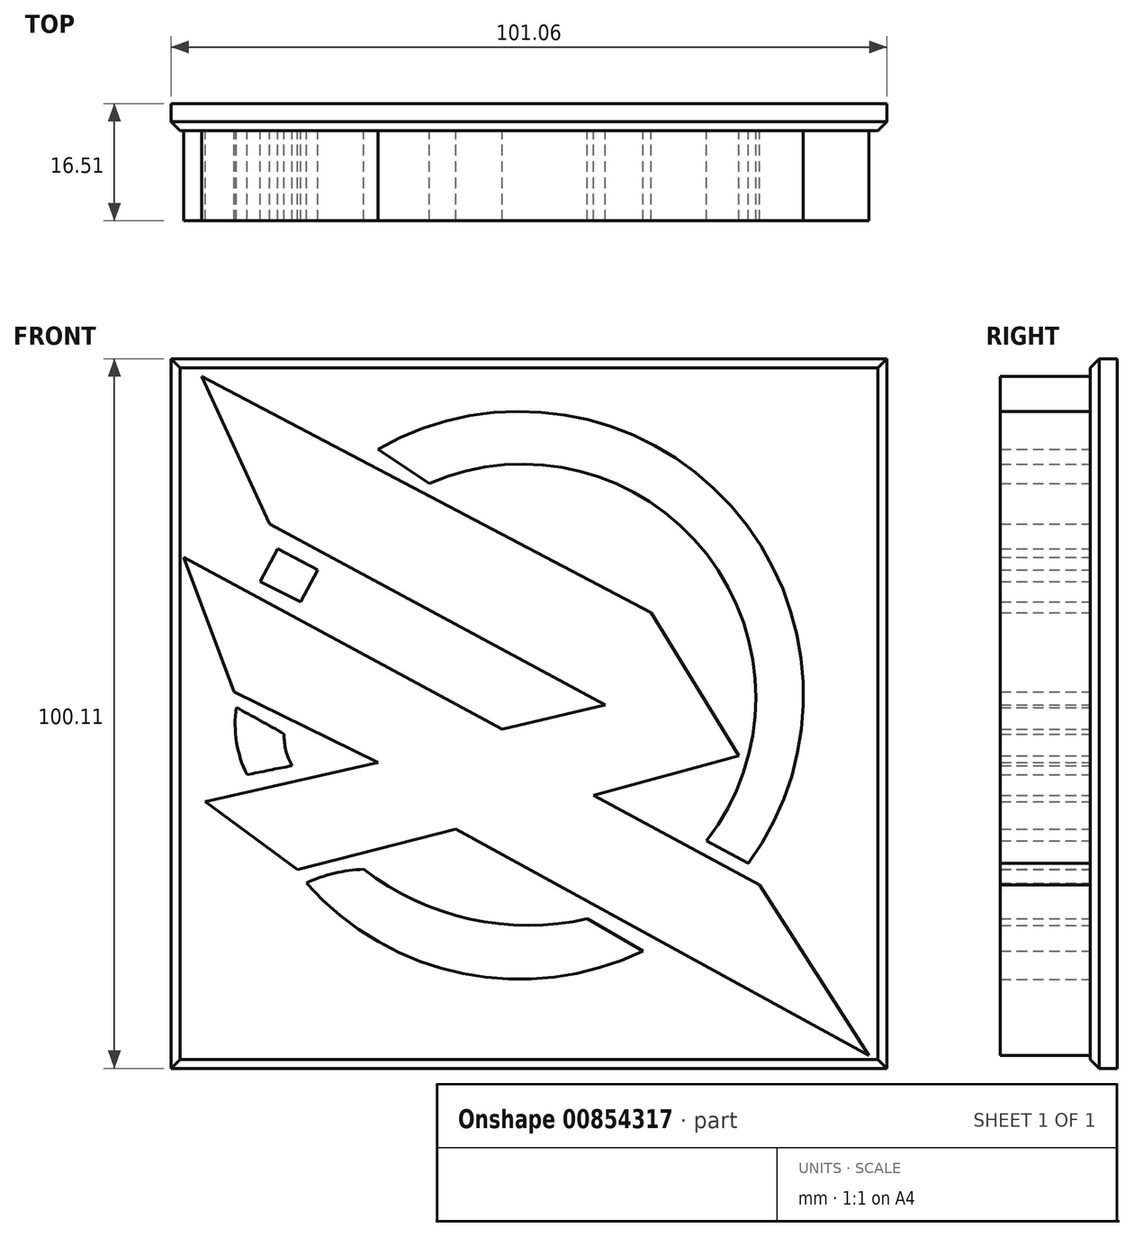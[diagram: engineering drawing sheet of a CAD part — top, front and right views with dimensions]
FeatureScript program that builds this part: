
annotation { "Feature Type Name" : "Feature", "Feature Type Description" : "" }
export const myFeature = defineFeature(function(context is Context, id is Id, definition is map)
    precondition{}
    {
        {
            var Q0;
            Q0=qCreatedBy(makeId("Front.planeOp"),FACE);
            var sketch = newSketch(context, id + "F0", { "sketchPlane" : qUnion([Q0])});
            skLineSegment(sketch, "E0", {"start": v(-59.3, 47.9) * mm, "end": v(4.16, 14.55) * mm});
            skLineSegment(sketch, "E1", {"start": v(4.16, 14.55) * mm, "end": v(16.56, -5.63) * mm});
            skLineSegment(sketch, "E2", {"start": v(16.56, -5.63) * mm, "end": v(-3.96, -11.27) * mm});
            skLineSegment(sketch, "E3", {"start": v(-3.96, -11.27) * mm, "end": v(19.5, -23.9) * mm});
            skLineSegment(sketch, "E4", {"start": v(19.5, -23.9) * mm, "end": v(34.87, -47.92) * mm});
            skLineSegment(sketch, "E5", {"start": v(34.87, -47.92) * mm, "end": v(-23.42, -16.04) * mm});
            skLineSegment(sketch, "E6", {"start": v(-23.42, -16.04) * mm, "end": v(-45.77, -21.75) * mm});
            skLineSegment(sketch, "E7", {"start": v(-45.77, -21.75) * mm, "end": v(-58.78, -12.17) * mm});
            skLineSegment(sketch, "E8", {"start": v(-58.78, -12.17) * mm, "end": v(-34.38, -6.6) * mm});
            skLineSegment(sketch, "E9", {"start": v(-34.38, -6.6) * mm, "end": v(-54.72, 3.38) * mm});
            skLineSegment(sketch, "E10", {"start": v(-54.72, 3.38) * mm, "end": v(-61.85, 22.32) * mm});
            skLineSegment(sketch, "E11", {"start": v(-61.85, 22.32) * mm, "end": v(-16.89, -1.91) * mm});
            skLineSegment(sketch, "E12", {"start": v(-16.89, -1.91) * mm, "end": v(-2.3, 1.51) * mm});
            skLineSegment(sketch, "E13", {"start": v(-2.3, 1.51) * mm, "end": v(-49.7, 27.04) * mm});
            skLineSegment(sketch, "E14", {"start": v(-49.7, 27.04) * mm, "end": v(-59.3, 47.9) * mm});
            skArc(sketch, "E15", {"start": v(-47.62, -2.6) * mm, "mid": v(-47.38, -4.92) * mm, "end": v(-46.5, -7.07) * mm});
            skArc(sketch, "E16", {"start": v(-47.62, -2.6) * mm, "mid": v(-50.99, -0.7) * mm, "end": v(-54.4, 1.14) * mm});
            skArc(sketch, "E17", {"start": v(-54.4, 1.14) * mm, "mid": v(-54.36, -3.72) * mm, "end": v(-52.88, -8.35) * mm});
            skArc(sketch, "E18", {"start": v(-46.5, -7.07) * mm, "mid": v(-49.7, -7.7) * mm, "end": v(-52.88, -8.35) * mm});
            skArc(sketch, "E19", {"start": v(-44.5, -23.6) * mm, "mid": v(-22.35, -36.42) * mm, "end": v(3.04, -33.21) * mm});
            skLineSegment(sketch, "E20", {"start": v(3.04, -33.21) * mm, "end": v(-4.83, -28.67) * mm});
            skArc(sketch, "E21", {"start": v(-36.42, -21.67) * mm, "mid": v(-21.4, -28.7) * mm, "end": v(-4.83, -28.67) * mm});
            skArc(sketch, "E22", {"start": v(-36.42, -21.67) * mm, "mid": v(-40.55, -22.25) * mm, "end": v(-44.5, -23.6) * mm});
            skLineSegment(sketch, "E23", {"start": v(17.88, -20.86) * mm, "end": v(11.97, -17.68) * mm});
            skArc(sketch, "E24", {"start": v(11.97, -17.68) * mm, "mid": v(12.02, 22.77) * mm, "end": v(-27.18, 32.75) * mm});
            skLineSegment(sketch, "E25", {"start": v(-34.38, 37.6) * mm, "end": v(-27.18, 32.75) * mm});
            skLineSegment(sketch, "E26", {"start": v(-45.34, 16.04) * mm, "end": v(-42.9, 20.55) * mm});
            skLineSegment(sketch, "E27", {"start": v(-42.9, 20.55) * mm, "end": v(-48.57, 23.53) * mm});
            skLineSegment(sketch, "E28", {"start": v(-48.57, 23.53) * mm, "end": v(-51, 18.91) * mm});
            skLineSegment(sketch, "E29", {"start": v(-51, 18.91) * mm, "end": v(-45.34, 16.04) * mm});
            skArc(sketch, "E30.trimOffspring", {"start": v(17.88, -20.86) * mm, "mid": v(15.46, 29.56) * mm, "end": v(-34.38, 37.6) * mm});
            skLineSegment(sketch, "E31", {"start": v(-27.18, 32.75) * mm, "end": v(-28.04, 31.47) * mm});
            skLineSegment(sketch, "E32", {"start": v(-27.93, 33.26) * mm, "end": v(-28.85, 31.9) * mm});
            skLineSegment(sketch, "E33", {"start": v(-34.38, 37.6) * mm, "end": v(-35.78, 35.53) * mm});
            skLineSegment(sketch, "E34", {"start": v(-33.82, 37.23) * mm, "end": v(-35.18, 35.22) * mm});
            skLineSegment(sketch, "E35", {"start": v(-49.7, 27.04) * mm, "end": v(-48.57, 23.53) * mm});
            skLineSegment(sketch, "E36", {"start": v(-51, 18.91) * mm, "end": v(-52.02, 17.02) * mm});
            skLineSegment(sketch, "E37", {"start": v(-50, 18.4) * mm, "end": v(-51.03, 16.49) * mm});
            skLineSegment(sketch, "E38", {"start": v(-54.72, 3.38) * mm, "end": v(-54.4, 1.14) * mm});
            skLineSegment(sketch, "E39", {"start": v(-53.62, 2.84) * mm, "end": v(-53.3, 0.56) * mm});
            skLineSegment(sketch, "E40", {"start": v(-47.5, 25.85) * mm, "end": v(-47.2, 22.81) * mm});
            skLineSegment(sketch, "E41", {"start": v(-44.5, -23.6) * mm, "end": v(-45.77, -21.75) * mm});
            skLineSegment(sketch, "E42", {"start": v(-44.03, -21.3) * mm, "end": v(-43.55, -23.2) * mm});
            skLineSegment(sketch, "E43", {"start": v(17.88, -20.86) * mm, "end": v(19.5, -23.9) * mm});
            skLineSegment(sketch, "E44", {"start": v(16.73, -20.24) * mm, "end": v(16.51, -22.3) * mm});
            skSolve(sketch);
        }
        {
            var Q0;
            {var subQ18=sQuery(id+"F0.wireOp",EDGE,"E1");Q0=makeQuery(id+"F0.imprint","IMPRINT",FACE,{"disambiguationData":[TD([[makeQuery(id+"F0.imprint","IMPRINT",EDGE,{"derivedFrom":subQ18}),-1.0]])]});}
            var Q1;
            {var subQ3=sQuery(id+"F0.wireOp",EDGE,"E15");Q1=makeQuery(id+"F0.imprint","IMPRINT",FACE,{"disambiguationData":[TD([[makeQuery(id+"F0.imprint","IMPRINT",EDGE,{"derivedFrom":subQ3}),-1.0]])]});}
            var Q2;
            {var subQ3=sQuery(id+"F0.wireOp",EDGE,"E26");Q2=makeQuery(id+"F0.imprint","IMPRINT",FACE,{"disambiguationData":[TD([[makeQuery(id+"F0.imprint","IMPRINT",EDGE,{"derivedFrom":subQ3}),1.0]])]});}
            var Q3;
            {var subQ3=sQuery(id+"F0.wireOp",EDGE,"E24");Q3=makeQuery(id+"F0.imprint","IMPRINT",FACE,{"disambiguationData":[TD([[makeQuery(id+"F0.imprint","IMPRINT",EDGE,{"derivedFrom":subQ3}),-1.0]])]});}
            var Q4;
            {var subQ3=sQuery(id+"F0.wireOp",EDGE,"E19");Q4=makeQuery(id+"F0.imprint","IMPRINT",FACE,{"disambiguationData":[TD([[makeQuery(id+"F0.imprint","IMPRINT",EDGE,{"derivedFrom":subQ3}),1.0]])]});}
            extrude(context, id + "F1", {"entities" : qUnion([Q0, Q1, Q2, Q3, Q4]), "depth" : 12.7 * mm, "offsetDistance" : 25.4 * mm});
        }
        {
            var Q0;
            Q0=makeQuery(id+"F1.opExtrude","CAP_FACE",FACE,{"disambiguationData":[OSD([sQuery(id+"F0.wireOp",EDGE,"E0"),sQuery(id+"F0.wireOp",EDGE,"E1"),sQuery(id+"F0.wireOp",EDGE,"E2"),sQuery(id+"F0.wireOp",EDGE,"E3"),sQuery(id+"F0.wireOp",EDGE,"E4"),sQuery(id+"F0.wireOp",EDGE,"E5"),sQuery(id+"F0.wireOp",EDGE,"E6"),sQuery(id+"F0.wireOp",EDGE,"E7"),sQuery(id+"F0.wireOp",EDGE,"E8"),sQuery(id+"F0.wireOp",EDGE,"E9"),sQuery(id+"F0.wireOp",EDGE,"E10"),sQuery(id+"F0.wireOp",EDGE,"E11"),sQuery(id+"F0.wireOp",EDGE,"E12"),sQuery(id+"F0.wireOp",EDGE,"E13"),sQuery(id+"F0.wireOp",EDGE,"E14")])],"isStart":true});
            var sketch = newSketch(context, id + "F2", { "sketchPlane" : qUnion([Q0])});
            skLineSegment(sketch, "E45.bottom", {"start": v(-37.45, -49.77) * mm, "end": v(63.6, -49.77) * mm});
            skLineSegment(sketch, "E45.top", {"start": v(-37.45, 50.34) * mm, "end": v(63.6, 50.34) * mm});
            skLineSegment(sketch, "E45.left", {"start": v(-37.45, -49.77) * mm, "end": v(-37.45, 50.34) * mm});
            skLineSegment(sketch, "E45.right", {"start": v(63.6, -49.77) * mm, "end": v(63.6, 50.34) * mm});
            skSolve(sketch);
        }
        {
            var Q0;
            Q0 = qSketchRegion(id + "F2", true);
            extrude(context, id + "F3", {"entities" : qUnion([Q0]), "depth" : 3.8 * mm, "offsetDistance" : 25.4 * mm});
        }
        {
            var Q0;
            Q0=makeQuery(id+"F3.opExtrude","CAP_EDGE",EDGE,{"disambiguationData":[OSD([sQuery(id+"F2.wireOp",EDGE,"E45.top")])],"isStart":true});
            var Q1;
            Q1=makeQuery(id+"F3.opExtrude","CAP_EDGE",EDGE,{"disambiguationData":[OSD([sQuery(id+"F2.wireOp",EDGE,"E45.right")])],"isStart":true});
            var Q2;
            Q2=makeQuery(id+"F3.opExtrude","CAP_EDGE",EDGE,{"disambiguationData":[OSD([sQuery(id+"F2.wireOp",EDGE,"E45.bottom")])],"isStart":true});
            var Q3;
            Q3=makeQuery(id+"F3.opExtrude","CAP_EDGE",EDGE,{"disambiguationData":[OSD([sQuery(id+"F2.wireOp",EDGE,"E45.left")])],"isStart":true});
            chamfer(context, id + "F4", {"entities" : qUnion([Q0, Q1, Q2, Q3]), "width" : 1.27 * mm, "tangentPropagation" : true});
        }
    });
